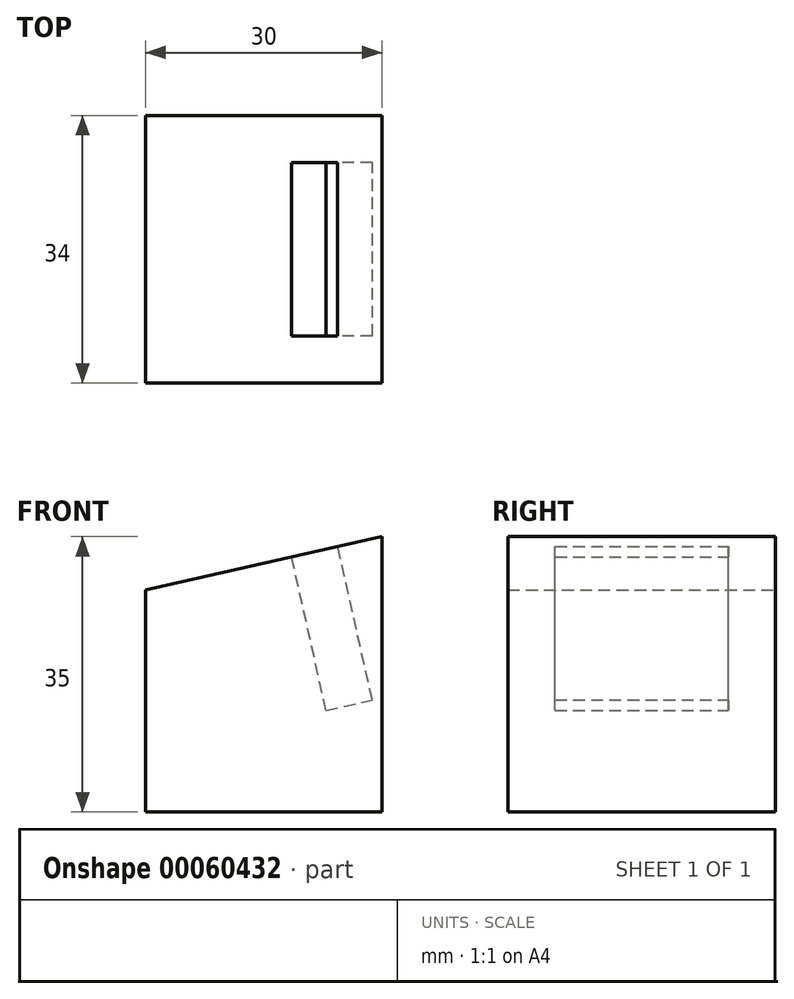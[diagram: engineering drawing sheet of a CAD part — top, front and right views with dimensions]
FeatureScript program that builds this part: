
annotation { "Feature Type Name" : "Feature", "Feature Type Description" : "" }
export const myFeature = defineFeature(function(context is Context, id is Id, definition is map)
    precondition{}
    {
        {
            var Q0;
            Q0=qCreatedBy(makeId("Front.planeOp"),FACE);
            var sketch = newSketch(context, id + "F0", { "sketchPlane" : qUnion([Q0])});
            skLineSegment(sketch, "E0", {"start": v(0, 0) * mm, "end": v(30, 0) * mm});
            skLineSegment(sketch, "E1", {"start": v(30, 0) * mm, "end": v(30, 35) * mm});
            skLineSegment(sketch, "E2", {"start": v(30, 35) * mm, "end": v(0, 28.23) * mm});
            skLineSegment(sketch, "E3", {"start": v(0, 28.23) * mm, "end": v(0, 0) * mm});
            skLineSegment(sketch, "E4", {"start": v(30, 0) * mm, "end": v(-125, 0) * mm, "construction": true});
            skLineSegment(sketch, "E5", {"start": v(-125, 0) * mm, "end": v(30, 35) * mm, "construction": true});
            skSolve(sketch);
        }
        {
            var Q0;
            Q0=makeQuery(id+"F0.imprint","IMPRINT",FACE,{"disambiguationData":[TD([[makeQuery(id+"F0.imprint","IMPRINT",EDGE,{"derivedFrom":sQuery(id+"F0.wireOp",EDGE,"E0")}),1.0]])]});
            extrude(context, id + "F1", {"entities" : qUnion([Q0]), "depth" : 34 * mm});
        }
        {
            var Q0;
            Q0=makeQuery(id+"F1.opExtrude","SWEPT_FACE",FACE,{"disambiguationData":[OSD([sQuery(id+"F0.wireOp",EDGE,"E2")])]});
            var sketch = newSketch(context, id + "F2", { "sketchPlane" : qUnion([Q0])});
            skLineSegment(sketch, "E6", {"start": v(6.22, -17) * mm, "end": v(36.97, -17) * mm, "construction": true});
            skLineSegment(sketch, "E7", {"start": v(30.97, -17) * mm, "end": v(30.97, -29) * mm});
            skLineSegment(sketch, "E8", {"start": v(30.97, -29) * mm, "end": v(36.97, -29) * mm});
            skLineSegment(sketch, "E9", {"start": v(30.97, -17) * mm, "end": v(30.97, -5) * mm});
            skLineSegment(sketch, "E10", {"start": v(30.97, -5) * mm, "end": v(36.97, -5) * mm});
            skLineSegment(sketch, "E11", {"start": v(36.97, -5) * mm, "end": v(36.97, -29) * mm});
            skLineSegment(sketch, "E12.bottom", {"start": v(25.22, -17) * mm, "end": v(31.22, -17) * mm, "construction": true});
            skLineSegment(sketch, "E12.top", {"start": v(25.22, -28) * mm, "end": v(31.22, -28) * mm});
            skLineSegment(sketch, "E12.left", {"start": v(25.22, -17) * mm, "end": v(25.22, -28) * mm});
            skLineSegment(sketch, "E12.right", {"start": v(31.22, -17) * mm, "end": v(31.22, -28) * mm});
            skLineSegment(sketch, "E13.bottom", {"start": v(31.22, -17) * mm, "end": v(25.22, -17) * mm, "construction": true});
            skLineSegment(sketch, "E13.top", {"start": v(31.22, -6) * mm, "end": v(25.22, -6) * mm});
            skLineSegment(sketch, "E13.left", {"start": v(31.22, -17) * mm, "end": v(31.22, -6) * mm});
            skLineSegment(sketch, "E13.right", {"start": v(25.22, -17) * mm, "end": v(25.22, -6) * mm});
            skSolve(sketch);
        }
        {
            var Q0;
            Q0=makeQuery(id+"F2.imprint","IMPRINT",FACE,{"disambiguationData":[TD([[makeQuery(id+"F2.imprint","IMPRINT",EDGE,{"derivedFrom":sQuery(id+"F2.wireOp",EDGE,"E13.bottom")}),-1.0]])]});
            var Q1;
            Q1=makeQuery(id+"F2.imprint","IMPRINT",FACE,{"disambiguationData":[TD([[makeQuery(id+"F2.imprint","IMPRINT",EDGE,{"derivedFrom":sQuery(id+"F2.wireOp",EDGE,"E12.top")}),1.0]])]});
            extrude(context, id + "F3", {"entities" : qUnion([Q0, Q1]), "operationType" : NewBodyOperationType.REMOVE, "oppositeDirection" : true, "depth" : 20 * mm});
        }
    });
